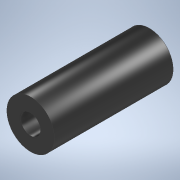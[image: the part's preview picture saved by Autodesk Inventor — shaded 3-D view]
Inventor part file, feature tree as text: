
AUTODESK INVENTOR PART (.ipt)
format: ipt  version: 2020 (Build 240168000, 168)  size: 100,864 bytes
history: native  units: in
note: dims shown in document units (in); Inventor stores cm internally (conversion verified against a paired STEP export)
features: extrude x1, sketch x1
ambient origin geometry x8: Origin, YZ Plane, XZ Plane, XY Plane, X Axis, Y Axis, Z Axis, Center Point
bodies: Solid1 (feature_tree)
feature tree (2):
  extrude  "Extrusion1"  Depth=1.25in
  sketch  "Sketch1"  dims[d0=0.21in d1=0.5in d2=1.25in d3=0.0in]
